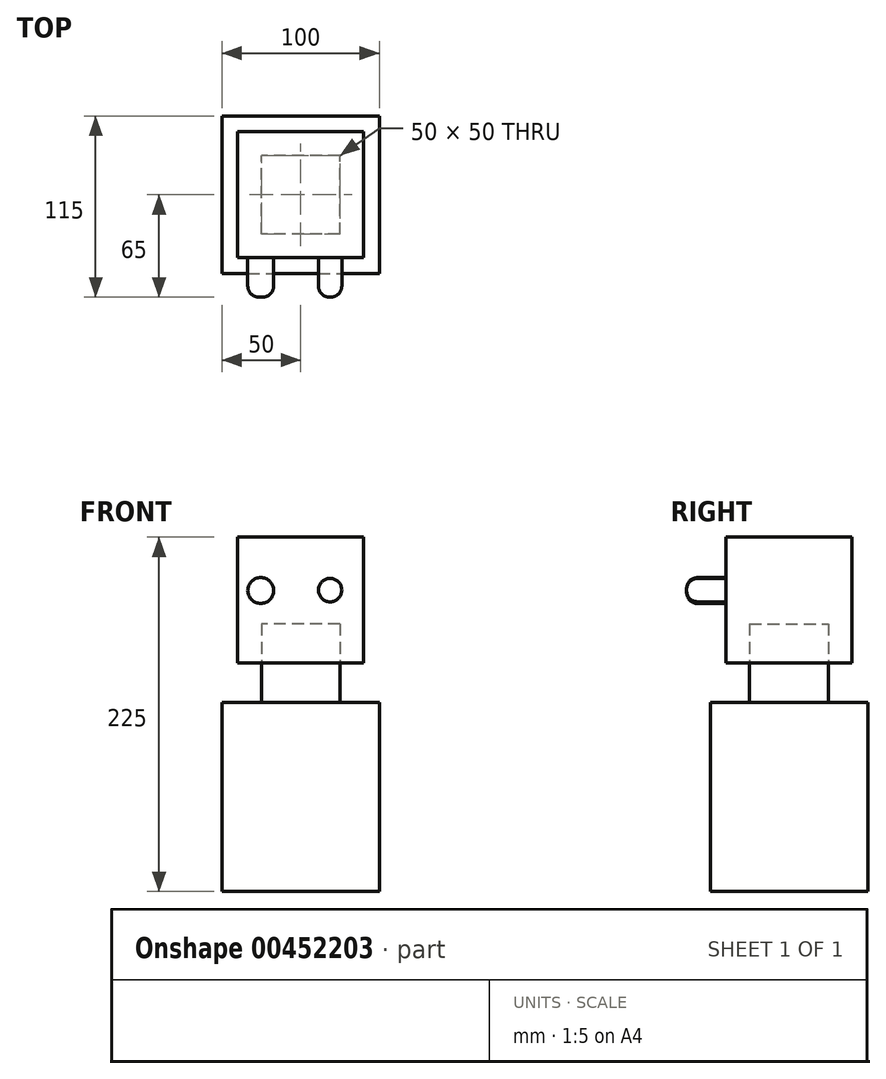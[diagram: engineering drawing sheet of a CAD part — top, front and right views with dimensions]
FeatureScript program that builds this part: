
annotation { "Feature Type Name" : "Feature", "Feature Type Description" : "" }
export const myFeature = defineFeature(function(context is Context, id is Id, definition is map)
    precondition{}
    {
        {
            var Q0;
            Q0=qCreatedBy(makeId("Top.planeOp"),FACE);
            var sketch = newSketch(context, id + "F0", { "sketchPlane" : qUnion([Q0])});
            skLineSegment(sketch, "E0.bottom", {"start": v(-50, 50) * mm, "end": v(50, 50) * mm});
            skLineSegment(sketch, "E0.top", {"start": v(-50, -50) * mm, "end": v(50, -50) * mm});
            skLineSegment(sketch, "E0.left", {"start": v(-50, 50) * mm, "end": v(-50, -50) * mm});
            skLineSegment(sketch, "E0.right", {"start": v(50, 50) * mm, "end": v(50, -50) * mm});
            skPoint(sketch, "E0.middle", {"position": v(0, 0) * mm});
            skSolve(sketch);
        }
        {
            var Q0;
            Q0=makeQuery(id+"F0.imprint","IMPRINT",FACE,{"disambiguationData":[TD([[makeQuery(id+"F0.imprint","IMPRINT",EDGE,{"derivedFrom":sQuery(id+"F0.wireOp",EDGE,"E0.bottom")}),-1.0]])]});
            extrude(context, id + "F1", {"entities" : qUnion([Q0]), "depth" : 120 * mm});
        }
        {
            var Q0;
            Q0=makeQuery(id+"F1.opExtrude","CAP_FACE",FACE,{"disambiguationData":[OSD([sQuery(id+"F0.wireOp",EDGE,"E0.bottom"),sQuery(id+"F0.wireOp",EDGE,"E0.top"),sQuery(id+"F0.wireOp",EDGE,"E0.left"),sQuery(id+"F0.wireOp",EDGE,"E0.right")])],"isStart":false});
            var sketch = newSketch(context, id + "F2", { "sketchPlane" : qUnion([Q0])});
            skLineSegment(sketch, "E1.bottom", {"start": v(25, -25) * mm, "end": v(-25, -25) * mm});
            skLineSegment(sketch, "E1.top", {"start": v(25, 25) * mm, "end": v(-25, 25) * mm});
            skLineSegment(sketch, "E1.left", {"start": v(25, -25) * mm, "end": v(25, 25) * mm});
            skLineSegment(sketch, "E1.right", {"start": v(-25, -25) * mm, "end": v(-25, 25) * mm});
            skPoint(sketch, "E1.middle", {"position": v(0, 0) * mm});
            skSolve(sketch);
        }
        {
            var Q0;
            Q0=makeQuery(id+"F2.imprint","IMPRINT",FACE,{"disambiguationData":[TD([[makeQuery(id+"F2.imprint","IMPRINT",EDGE,{"derivedFrom":sQuery(id+"F2.wireOp",EDGE,"E1.bottom")}),-1.0]])]});
            extrude(context, id + "F3", {"entities" : qUnion([Q0]), "operationType" : NewBodyOperationType.ADD, "depth" : 50 * mm});
        }
        {
            var Q0;
            Q0=qCreatedBy(makeId("Top.planeOp"),FACE);
            cPlane(context, id + "F4", {"entities" : qUnion([Q0]), "cplaneType" : CPlaneType.OFFSET, "offset" : 145 * mm, "width" : 150 * mm, "height" : 150 * mm});
        }
        {
            var Q0;
            Q0=qCreatedBy(id+"F4.planeOp",FACE);
            var sketch = newSketch(context, id + "F5", { "sketchPlane" : qUnion([Q0])});
            skLineSegment(sketch, "E2.bottom", {"start": v(-40, 40) * mm, "end": v(40, 40) * mm});
            skLineSegment(sketch, "E2.top", {"start": v(-40, -40) * mm, "end": v(40, -40) * mm});
            skLineSegment(sketch, "E2.left", {"start": v(-40, 40) * mm, "end": v(-40, -40) * mm});
            skLineSegment(sketch, "E2.right", {"start": v(40, 40) * mm, "end": v(40, -40) * mm});
            skPoint(sketch, "E2.middle", {"position": v(0, 0) * mm});
            skSolve(sketch);
        }
        {
            var Q0;
            Q0=makeQuery(id+"F5.imprint","IMPRINT",FACE,{"disambiguationData":[TD([[makeQuery(id+"F5.imprint","IMPRINT",EDGE,{"derivedFrom":sQuery(id+"F5.wireOp",EDGE,"E2.bottom")}),-1.0]])]});
            extrude(context, id + "F6", {"entities" : qUnion([Q0]), "depth" : 80 * mm});
        }
        {
            var Q0;
            Q0=makeQuery(id+"F1.opExtrude","SWEPT_BODY",BODY,{"disambiguationData":[OSD([sQuery(id+"F0.wireOp",EDGE,"E0.bottom"),sQuery(id+"F0.wireOp",EDGE,"E0.top"),sQuery(id+"F0.wireOp",EDGE,"E0.left"),sQuery(id+"F0.wireOp",EDGE,"E0.right")])]});
            var Q1;
            Q1=makeQuery(id+"F6.opExtrude","SWEPT_BODY",BODY,{"disambiguationData":[OSD([sQuery(id+"F5.wireOp",EDGE,"E2.bottom"),sQuery(id+"F5.wireOp",EDGE,"E2.top"),sQuery(id+"F5.wireOp",EDGE,"E2.left"),sQuery(id+"F5.wireOp",EDGE,"E2.right")])]});
            booleanBodies(context, id + "F7", {"operationType" : BooleanOperationType.SUBTRACTION, "tools" : qUnion([Q0]), "targets" : qUnion([Q1]), "keepTools" : true});
        }
        {
            var Q0;
            Q0=makeQuery(id+"F6.opExtrude","SWEPT_FACE",FACE,{"disambiguationData":[OSD([sQuery(id+"F5.wireOp",EDGE,"E2.top")])]});
            var sketch = newSketch(context, id + "F8", { "sketchPlane" : qUnion([Q0])});
            skCircle(sketch, "E3", {"center": v(-25.43, 191.11) * mm, "radius": 8.2 * mm});
            skCircle(sketch, "E4", {"center": v(18.67, 191.4) * mm, "radius": 7.42 * mm});
            skSolve(sketch);
        }
        {
            var Q0;
            Q0=makeQuery(id+"F8.imprint","IMPRINT",FACE,{"disambiguationData":[TD([[makeQuery(id+"F8.imprint","IMPRINT",EDGE,{"derivedFrom":sQuery(id+"F8.wireOp",EDGE,"E3")}),1.0]])]});
            var Q1;
            Q1=makeQuery(id+"F8.imprint","IMPRINT",FACE,{"disambiguationData":[TD([[makeQuery(id+"F8.imprint","IMPRINT",EDGE,{"derivedFrom":sQuery(id+"F8.wireOp",EDGE,"E4")}),1.0]])]});
            extrude(context, id + "F9", {"entities" : qUnion([Q0, Q1]), "depth" : 25 * mm});
        }
        {
            var Q0;
            Q0=makeQuery(id+"F9.opExtrude","CAP_EDGE",EDGE,{"disambiguationData":[OSD([sQuery(id+"F8.wireOp",EDGE,"E3")])],"isStart":false});
            var Q1;
            Q1=makeQuery(id+"F9.opExtrude","CAP_EDGE",EDGE,{"disambiguationData":[OSD([sQuery(id+"F8.wireOp",EDGE,"E4")])],"isStart":false});
            fillet(context, id + "F10", {"entities" : qUnion([Q0, Q1]), "radius" : 7 * mm, "tangentPropagation" : true, "allowEdgeOverflow" : false});
        }
    });
